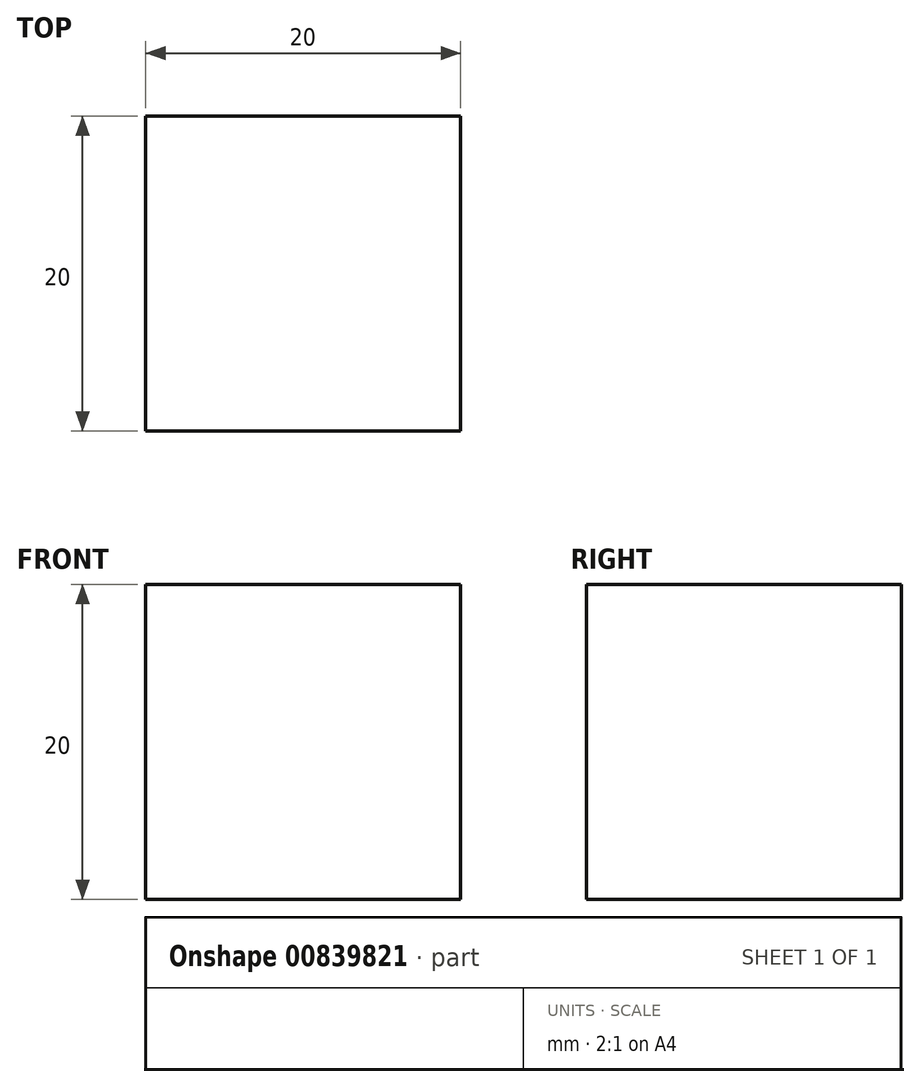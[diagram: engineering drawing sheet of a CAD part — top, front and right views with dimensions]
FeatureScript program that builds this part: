
annotation { "Feature Type Name" : "Feature", "Feature Type Description" : "" }
export const myFeature = defineFeature(function(context is Context, id is Id, definition is map)
    precondition{}
    {
        {
            var Q0;
            Q0=qCreatedBy(makeId("Top.planeOp"),FACE);
            var sketch = newSketch(context, id + "F0", { "sketchPlane" : qUnion([Q0])});
            skLineSegment(sketch, "E0.bottom", {"start": v(-10, -10) * mm, "end": v(10, -10) * mm});
            skLineSegment(sketch, "E0.top", {"start": v(-10, 10) * mm, "end": v(10, 10) * mm});
            skLineSegment(sketch, "E0.left", {"start": v(-10, -10) * mm, "end": v(-10, 10) * mm});
            skLineSegment(sketch, "E0.right", {"start": v(10, -10) * mm, "end": v(10, 10) * mm});
            skLineSegment(sketch, "E1", {"start": v(-10, -10) * mm, "end": v(10, 10) * mm, "construction": true});
            skSolve(sketch);
        }
        {
            var Q0;
            Q0 = qSketchRegion(id + "F0", true);
            extrude(context, id + "F1", {"entities" : qUnion([Q0]), "depth" : 20 * mm, "offsetDistance" : 25 * mm});
        }
    });
